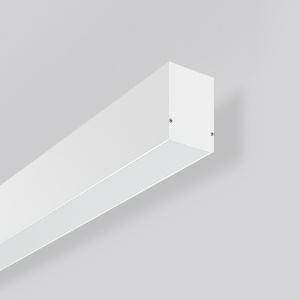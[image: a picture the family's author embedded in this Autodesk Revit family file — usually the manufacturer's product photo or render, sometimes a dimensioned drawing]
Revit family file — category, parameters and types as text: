
# Revit family: less_is_more_50_312606_002_1_b3bf
name_source: partatom
category: Lighting Fixtures
units: mm (PartAtom-declared; Revit-internal decimal feet)

## family parameters
Cut with Voids When Loaded = No
Host = Face
Light Source = No
Part Type = Normal
Room Calculation Point = No
Round Connector Dimension = Use Diameter
Shared = No

## types (1)
- LESS IS MORE 50 (1 x LED Modul 840, 2050 lm, 4000)
    Apparent Load = 15 VA
    CIE Flux Codes = 48 80 96 50 100
    Color Rendering = 80
    Color Temperature = 4000
    Default Elevation = 1800 mm
    Description = Series: LESS IS MORE 50
Linear wall luminaires. Housing: extruded aluminium profile, powder-coated. End cap aluminium powder-coated. Diffuser made of non-yellowing plastic (PMMA), opal. Direct 50%, indirect 50% light emission. Suitable for Wall (surface). LED unit with integrated converter interchangeable and removable. Suitable for through-wiring. With sensors or as a safety luminaire on request. 
Colour: traffic white, matt (RAL 9016)
Length: 847 mm
Width: 67 mm
Height: 75 mm
Lamp: LED
Socket: without socket
Colour temperature: 4000K
Colour rendering index (CRI): 80
Light source: LED
Socket lamp2: Without base
Colour temperature: 4000K
Colour rendering index (CRI) 2: 80
System power: 15 W
Rated luminous flux: 2050 lm
Luminous efficiency: 137 lm/W
Control gear: Regulated power supply
Control gear: Regulated power supply
Protection class: I
Type of protection: IP 20
    Height = 75 mm
    Lamp = 1 x LED Modul 840
    Lamp Light Flux = 2050 lm
    Lamp count = 1
    Length = 847 mm
    Lifetime = 50000 h
    Luminous efficacy = 137 lm/W
    Manufacturer = RZB
    ModVariant = No
    Model = 312606.002.1
    Mounting Place = Wall
    Mounting Type = Surface mounted
    Number of Poles = 1
    OnlyDefault = Yes
    Power Factor = 1
    Product Name = LESS IS MORE 50
    Product group = Surface mounted LED linear luminaires
    ProductGroupID = 2007
    Protection Class = Protection class I
    Protection Degree = IP 20
    RLX_Detail_Level = 1
    RLX_Emergency_Light_Flux = 0 lm
    RLX_Emergency_Type = 0
    RLX_Emergency_Type_DB = No
    RlxData = <blob elided: 39613 chars, md5=189192a5>
    Socket = socket
    Standby Power = 0 W
    System Light Flux = 2050 lm
    System Power = 15 W
    Type Comments = Product without accessories
    Type Image = 312606.002.jpg
    URL = http://relux.com
    VarID = ---
    Voltage = 0 V
    Weight = 0.00 kg
    Width = 67 mm

## geometry (parser evidence)
native form markers: Blend x4, Sweep x14
no freeform markers — native parametric forms only
